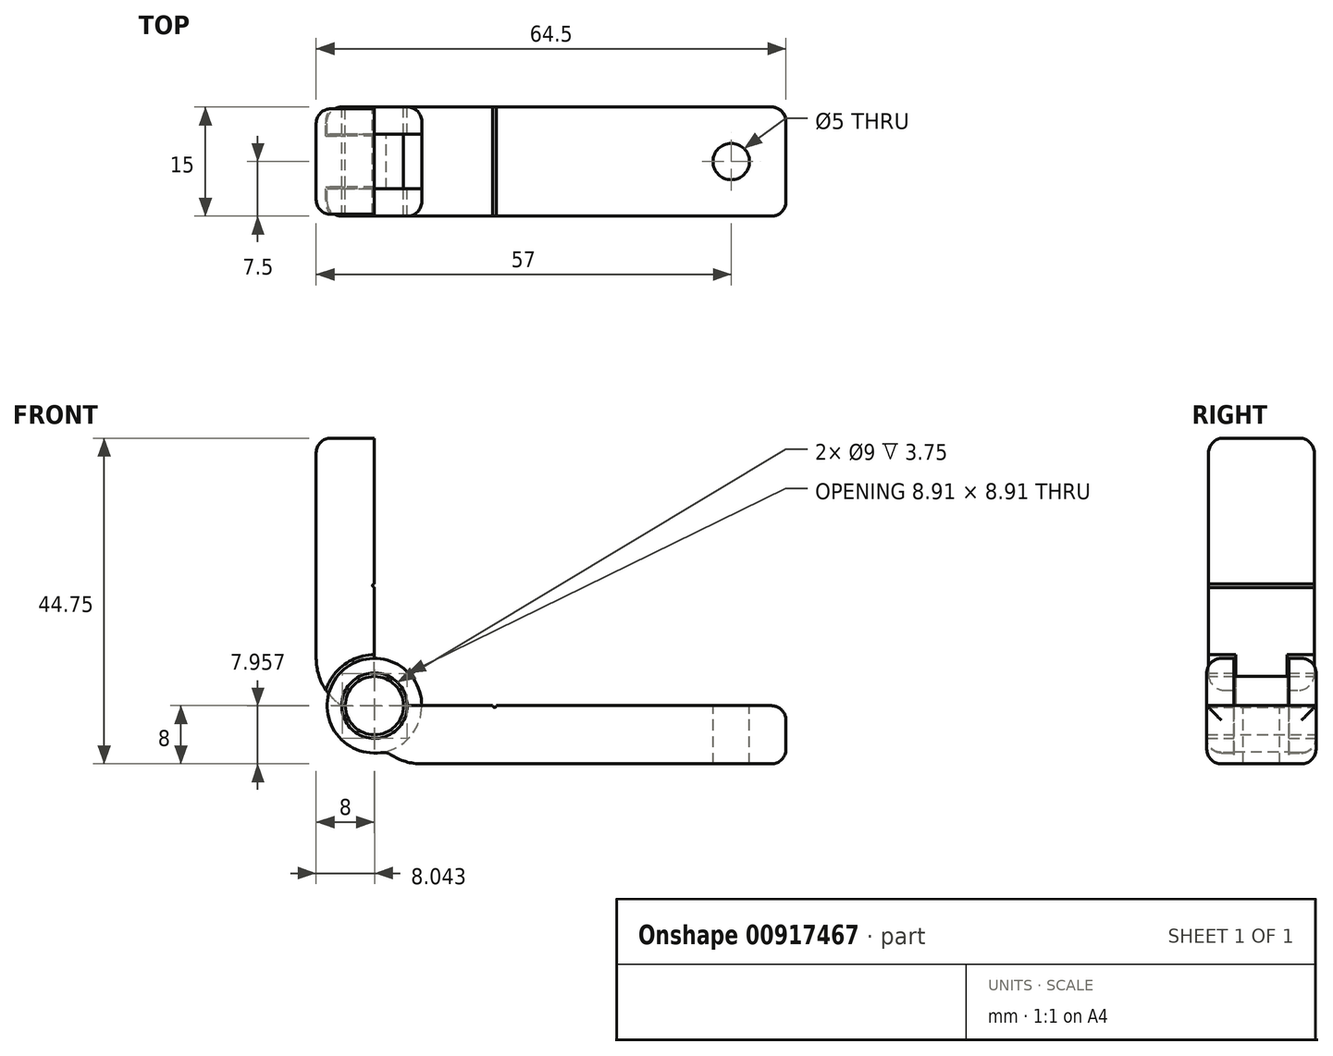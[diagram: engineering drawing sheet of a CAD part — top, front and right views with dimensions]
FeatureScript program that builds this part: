
annotation { "Feature Type Name" : "Feature", "Feature Type Description" : "" }
export const myFeature = defineFeature(function(context is Context, id is Id, definition is map)
    precondition{}
    {
        {
            var Q0;
            Q0=qCreatedBy(makeId("Front.planeOp"),FACE);
            var sketch = newSketch(context, id + "F0", { "sketchPlane" : qUnion([Q0])});
            skLineSegment(sketch, "E0.bottom", {"start": v(0, 0) * mm, "end": v(50, 0) * mm});
            skLineSegment(sketch, "E0.top", {"start": v(0, 8) * mm, "end": v(9.75, 8) * mm});
            skLineSegment(sketch, "E0.left", {"start": v(0, 0) * mm, "end": v(0, 8) * mm});
            skLineSegment(sketch, "E0.right", {"start": v(50, 0) * mm, "end": v(50, 8) * mm});
            skArc(sketch, "E1", {"start": v(9.75, 8) * mm, "mid": v(10, 7.75) * mm, "end": v(10.25, 8) * mm});
            skLineSegment(sketch, "E2.trimOffspring", {"start": v(10.25, 8) * mm, "end": v(50, 8) * mm});
            skLineSegment(sketch, "E3", {"start": v(0, 8) * mm, "end": v(-31.98, 8) * mm, "construction": true});
            skCircle(sketch, "E4", {"center": v(-6.5, 8) * mm, "radius": 4 * mm});
            skCircle(sketch, "E5", {"center": v(-6.5, 8) * mm, "radius": 4.5 * mm});
            skPoint(sketch, "E6", {"position": v(-2, 8) * mm});
            skPoint(sketch, "E7", {"position": v(-6.5, 12.5) * mm});
            skLineSegment(sketch, "E8.bottom", {"start": v(-6.5, 14.5) * mm, "end": v(-14.5, 14.5) * mm});
            skLineSegment(sketch, "E8.top", {"start": v(-6.5, 44.75) * mm, "end": v(-14.5, 44.75) * mm});
            skLineSegment(sketch, "E8.left", {"start": v(-6.5, 14.5) * mm, "end": v(-6.5, 24.25) * mm});
            skLineSegment(sketch, "E8.right", {"start": v(-14.5, 14.5) * mm, "end": v(-14.5, 44.75) * mm});
            skArc(sketch, "E9", {"start": v(-6.5, 24.75) * mm, "mid": v(-6.75, 24.5) * mm, "end": v(-6.5, 24.25) * mm});
            skLineSegment(sketch, "E10.trimOffspring", {"start": v(-6.5, 24.75) * mm, "end": v(-6.5, 44.75) * mm});
            skLineSegment(sketch, "E11", {"start": v(-2, 8) * mm, "end": v(0, 8) * mm});
            skPoint(sketch, "E12", {"position": v(-6.5, 3.5) * mm});
            skArc(sketch, "E13", {"start": v(-6.5, 3.5) * mm, "mid": v(-3.7, 0.93) * mm, "end": v(0, 0) * mm});
            skPoint(sketch, "E14", {"position": v(-11, 8) * mm});
            skArc(sketch, "E15", {"start": v(-14.5, 14.5) * mm, "mid": v(-13.57, 10.8) * mm, "end": v(-11, 8) * mm});
            skLineSegment(sketch, "E16", {"start": v(-6.5, 12.5) * mm, "end": v(-6.5, 14.5) * mm});
            skLineSegment(sketch, "E17", {"start": v(-6.5, 12.5) * mm, "end": v(-6.5, 12) * mm});
            skLineSegment(sketch, "E18", {"start": v(-11, 8) * mm, "end": v(-10.5, 8) * mm});
            skCircle(sketch, "E19", {"center": v(-6.5, 8) * mm, "radius": 6.5 * mm});
            skSolve(sketch);
        }
        {
            var Q0;
            Q0=makeQuery(id+"F0.imprint","IMPRINT",FACE,{"disambiguationData":[TD([[makeQuery(id+"F0.imprint","IMPRINT",EDGE,{"derivedFrom":sQuery(id+"F0.wireOp",EDGE,"E0.bottom")}),1.0]])]});
            var Q1;
            Q1=makeQuery(id+"F0.imprint","IMPRINT",FACE,{"disambiguationData":[TD([[makeQuery(id+"F0.imprint","IMPRINT",EDGE,{"derivedFrom":sQuery(id+"F0.wireOp",EDGE,"E0.left")}),1.0]])]});
            var Q2;
            {var subQ0=sQuery(id+"F0.wireOp",EDGE,"E11");Q2=makeQuery(id+"F0.imprint","IMPRINT",FACE,{"disambiguationData":[TD([[makeQuery(id+"F0.imprint","IMPRINT",EDGE,{"derivedFrom":subQ0}),-1.0]])]});}
            var Q3;
            {var subQ0=sQuery(id+"F0.wireOp",EDGE,"E11");Q3=makeQuery(id+"F0.imprint","IMPRINT",FACE,{"disambiguationData":[TD([[makeQuery(id+"F0.imprint","IMPRINT",EDGE,{"derivedFrom":subQ0}),1.0]])]});}
            var Q4;
            {var subQ3=sQuery(id+"F0.wireOp",EDGE,"E16");Q4=makeQuery(id+"F0.imprint","IMPRINT",FACE,{"disambiguationData":[TD([[makeQuery(id+"F0.imprint","IMPRINT",EDGE,{"derivedFrom":subQ3}),1.0]])]});}
            var Q5;
            {var subQ0=sQuery(id+"F0.wireOp",EDGE,"E13");var subQ1=sQuery(id+"F0.wireOp",EDGE,"E5");var subQ2=makeQuery(id+"F0.imprint","INTERSECT",VERTEX,{"derivedFrom":[subQ1,subQ0]});Q5=makeQuery(id+"F0.imprint","IMPRINT",FACE,{"disambiguationData":[TD([[makeQuery(id+"F0.imprint","IMPRINT",EDGE,{"disambiguationData":[TD([[subQ2,-1.0]])],"derivedFrom":subQ0}),-1.0]])]});}
            extrude(context, id + "F1", {"entities" : qUnion([Q0, Q1, Q2, Q3, Q4, Q5]), "depth" : 7.5 * mm, "offsetDistance" : 25 * mm, "hasSecondDirection" : true, "secondDirectionOppositeDirection" : true, "secondDirectionDepth" : 7.5 * mm});
        }
        {
            var Q0;
            {var subQ0=sQuery(id+"F0.wireOp",EDGE,"E11");Q0=makeQuery(id+"F0.imprint","IMPRINT",FACE,{"disambiguationData":[TD([[makeQuery(id+"F0.imprint","IMPRINT",EDGE,{"derivedFrom":subQ0}),1.0]])]});}
            var Q1;
            {var subQ3=sQuery(id+"F0.wireOp",EDGE,"E16");Q1=makeQuery(id+"F0.imprint","IMPRINT",FACE,{"disambiguationData":[TD([[makeQuery(id+"F0.imprint","IMPRINT",EDGE,{"derivedFrom":subQ3}),1.0]])]});}
            var Q2;
            {var subQ0=sQuery(id+"F0.wireOp",EDGE,"E13");var subQ1=sQuery(id+"F0.wireOp",EDGE,"E5");var subQ2=makeQuery(id+"F0.imprint","INTERSECT",VERTEX,{"derivedFrom":[subQ1,subQ0]});Q2=makeQuery(id+"F0.imprint","IMPRINT",FACE,{"disambiguationData":[TD([[makeQuery(id+"F0.imprint","IMPRINT",EDGE,{"disambiguationData":[TD([[subQ2,-1.0]])],"derivedFrom":subQ0}),-1.0]])]});}
            var Q3;
            {var subQ0=sQuery(id+"F0.wireOp",EDGE,"E11");Q3=makeQuery(id+"F0.imprint","IMPRINT",FACE,{"disambiguationData":[TD([[makeQuery(id+"F0.imprint","IMPRINT",EDGE,{"derivedFrom":subQ0}),-1.0]])]});}
            extrude(context, id + "F2", {"entities" : qUnion([Q0, Q1, Q2, Q3]), "operationType" : NewBodyOperationType.REMOVE, "oppositeDirection" : true, "depth" : 3.75 * mm, "offsetDistance" : 25 * mm, "hasSecondDirection" : true, "secondDirectionOppositeDirection" : false, "secondDirectionDepth" : 3.75 * mm});
        }
        {
            var Q0;
            Q0=makeQuery(id+"F0.imprint","IMPRINT",FACE,{"disambiguationData":[TD([[makeQuery(id+"F0.imprint","IMPRINT",EDGE,{"derivedFrom":sQuery(id+"F0.wireOp",EDGE,"E8.bottom")}),-1.0]])]});
            var Q1;
            Q1=makeQuery(id+"F0.imprint","IMPRINT",FACE,{"disambiguationData":[TD([[makeQuery(id+"F0.imprint","IMPRINT",EDGE,{"derivedFrom":sQuery(id+"F0.wireOp",EDGE,"E8.bottom")}),1.0]])]});
            var Q2;
            {var subQ3=sQuery(id+"F0.wireOp",EDGE,"E16");Q2=makeQuery(id+"F0.imprint","IMPRINT",FACE,{"disambiguationData":[TD([[makeQuery(id+"F0.imprint","IMPRINT",EDGE,{"derivedFrom":subQ3}),1.0]])]});}
            var Q3;
            {var subQ0=sQuery(id+"F0.wireOp",EDGE,"E4");var subQ1=makeQuery(id+"F0.imprint","INTERSECT",VERTEX,{"derivedFrom":[subQ0,sQuery(id+"F0.wireOp",EDGE,"E17")]});Q3=makeQuery(id+"F0.imprint","IMPRINT",FACE,{"disambiguationData":[TD([[makeQuery(id+"F0.imprint","IMPRINT",EDGE,{"disambiguationData":[TD([[subQ1,-1.0]])],"derivedFrom":subQ0}),1.0]])]});}
            var Q4;
            {var subQ0=sQuery(id+"F0.wireOp",EDGE,"E17");Q4=makeQuery(id+"F0.imprint","IMPRINT",FACE,{"disambiguationData":[TD([[makeQuery(id+"F0.imprint","IMPRINT",EDGE,{"derivedFrom":subQ0}),-1.0]])]});}
            extrude(context, id + "F3", {"entities" : qUnion([Q0, Q1, Q2, Q3, Q4]), "depth" : 3.5 * mm, "offsetDistance" : 25 * mm, "hasSecondDirection" : true, "secondDirectionOppositeDirection" : true, "secondDirectionDepth" : 3.5 * mm});
        }
        {
            var Q0;
            {var subQ0=sQuery(id+"F0.wireOp",EDGE,"E4");var subQ1=makeQuery(id+"F0.imprint","INTERSECT",VERTEX,{"derivedFrom":[subQ0,sQuery(id+"F0.wireOp",EDGE,"E17")]});Q0=makeQuery(id+"F0.imprint","IMPRINT",FACE,{"disambiguationData":[TD([[makeQuery(id+"F0.imprint","IMPRINT",EDGE,{"disambiguationData":[TD([[subQ1,-1.0]])],"derivedFrom":subQ0}),1.0]])]});}
            extrude(context, id + "F4", {"entities" : qUnion([Q0]), "operationType" : NewBodyOperationType.ADD, "depth" : 7.5 * mm, "offsetDistance" : 25 * mm, "hasSecondDirection" : true, "secondDirectionOppositeDirection" : true, "secondDirectionDepth" : 7.5 * mm});
        }
        {
            var Q0;
            Q0=makeQuery(id+"F3.opExtrude","CAP_FACE",FACE,{"disambiguationData":[OSD([sQuery(id+"F0.wireOp",EDGE,"E4"),sQuery(id+"F0.wireOp",EDGE,"E8.top"),sQuery(id+"F0.wireOp",EDGE,"E8.left"),sQuery(id+"F0.wireOp",EDGE,"E8.right"),sQuery(id+"F0.wireOp",EDGE,"E9"),sQuery(id+"F0.wireOp",EDGE,"E10.trimOffspring"),sQuery(id+"F0.wireOp",EDGE,"E15"),sQuery(id+"F0.wireOp",EDGE,"E16"),sQuery(id+"F0.wireOp",EDGE,"E17"),sQuery(id+"F0.wireOp",EDGE,"E18")])],"isStart":false});
            var sketch = newSketch(context, id + "F5", { "sketchPlane" : qUnion([Q0])});
            skLineSegment(sketch, "E20.top", {"start": v(-6.5, 44.75) * mm, "end": v(-14.5, 44.75) * mm});
            skLineSegment(sketch, "E20.left", {"start": v(-6.5, 15) * mm, "end": v(-6.5, 24.25) * mm});
            skLineSegment(sketch, "E20.right", {"start": v(-14.5, 14.5) * mm, "end": v(-14.5, 44.75) * mm});
            skArc(sketch, "E21", {"start": v(-6.5, 24.75) * mm, "mid": v(-6.75, 24.5) * mm, "end": v(-6.5, 24.25) * mm});
            skLineSegment(sketch, "E22.trimOffspring", {"start": v(-6.5, 24.75) * mm, "end": v(-6.5, 44.75) * mm});
            skArc(sketch, "E23", {"start": v(-6.5, 15) * mm, "mid": v(-10.62, 13.66) * mm, "end": v(-13.16, 10.14) * mm});
            skArc(sketch, "E24", {"start": v(-14.5, 14.5) * mm, "mid": v(-14.16, 12.22) * mm, "end": v(-13.16, 10.14) * mm});
            skSolve(sketch);
        }
        {
            var Q0;
            Q0 = qSketchRegion(id + "F5", true);
            extrude(context, id + "F6", {"entities" : qUnion([Q0]), "operationType" : NewBodyOperationType.ADD, "depth" : 3.75 * mm, "offsetDistance" : 25 * mm, "hasSecondDirection" : true, "secondDirectionOppositeDirection" : true, "secondDirectionDepth" : 10.75 * mm});
        }
        {
            var Q0;
            Q0=makeQuery(id+"F1.opExtrude","CAP_EDGE",EDGE,{"disambiguationData":[OSD([sQuery(id+"F0.wireOp",EDGE,"E0.right")])],"isStart":false});
            var Q1;
            Q1=makeQuery(id+"F1.opExtrude","CAP_EDGE",EDGE,{"disambiguationData":[OSD([sQuery(id+"F0.wireOp",EDGE,"E0.right")])],"isStart":true});
            var Q2;
            Q2=makeQuery(id+"F1.opExtrude","SWEPT_EDGE",EDGE,{"disambiguationData":[OSD([sQuery(id+"F0.wireOp",EDGE,"E0.right"),sQuery(id+"F0.wireOp",EDGE,"E2.trimOffspring")])]});
            var Q3;
            Q3=makeQuery(id+"F1.opExtrude","SWEPT_EDGE",EDGE,{"disambiguationData":[OSD([sQuery(id+"F0.wireOp",EDGE,"E0.bottom"),sQuery(id+"F0.wireOp",EDGE,"E0.right")])]});
            var Q4;
            Q4=makeQuery(id+"F1.opExtrude","CAP_EDGE",EDGE,{"disambiguationData":[OSD([sQuery(id+"F0.wireOp",EDGE,"E0.bottom")])],"isStart":false});
            var Q5;
            Q5=makeQuery(id+"F1.opExtrude","CAP_EDGE",EDGE,{"disambiguationData":[OSD([sQuery(id+"F0.wireOp",EDGE,"E19")])],"isStart":false});
            var Q6;
            Q6=makeQuery(id+"F1.opExtrude","CAP_EDGE",EDGE,{"disambiguationData":[OSD([sQuery(id+"F0.wireOp",EDGE,"E0.bottom")])],"isStart":true});
            var Q7;
            Q7=makeQuery(id+"F1.opExtrude","CAP_EDGE",EDGE,{"disambiguationData":[OSD([sQuery(id+"F0.wireOp",EDGE,"E19")])],"isStart":true});
            var Q8;
            Q8=makeQuery(id+"F6.opExtrude","CAP_EDGE",EDGE,{"disambiguationData":[OSD([sQuery(id+"F5.wireOp",EDGE,"E20.right")])],"isStart":true});
            var Q9;
            Q9=makeQuery(id+"F6.opExtrude","CAP_EDGE",EDGE,{"disambiguationData":[OSD([sQuery(id+"F5.wireOp",EDGE,"E20.top")])],"isStart":true});
            var Q10;
            Q10=makeQuery(id+"F6.boolean.opBoolean","MERGE",EDGE,{"derivedFrom":[makeQuery(id+"F3.opExtrude","SWEPT_EDGE",EDGE,{"disambiguationData":[OSD([sQuery(id+"F0.wireOp",EDGE,"E8.top"),sQuery(id+"F0.wireOp",EDGE,"E8.right")])]}),makeQuery(id+"F6.opExtrude","SWEPT_EDGE",EDGE,{"disambiguationData":[OSD([sQuery(id+"F5.wireOp",EDGE,"E20.top"),sQuery(id+"F5.wireOp",EDGE,"E20.right")])]})]});
            var Q11;
            Q11=makeQuery(id+"F6.opExtrude","CAP_EDGE",EDGE,{"disambiguationData":[OSD([sQuery(id+"F5.wireOp",EDGE,"E20.top")])],"isStart":false});
            var Q12;
            Q12=makeQuery(id+"F6.opExtrude","CAP_EDGE",EDGE,{"disambiguationData":[OSD([sQuery(id+"F5.wireOp",EDGE,"E20.right")])],"isStart":false});
            var Q13;
            {var subQ0=sQuery(id+"F0.wireOp",EDGE,"E13");var subQ1=sQuery(id+"F0.wireOp",EDGE,"E19");Q13=makeQuery(id+"F2.boolean.opBoolean","SPLIT",EDGE,{"disambiguationData":[topologyDisambiguationEdgeConnected([makeQuery(id+"F1.opExtrude","SWEPT_FACE",FACE,{"disambiguationData":[OSD([subQ0])]}),makeQuery(id+"F2.opExtrude","SWEPT_FACE",FACE,{"disambiguationData":[OSD([subQ1])]})])],"derivedFrom":makeQuery(id+"F1.opExtrude","SWEPT_EDGE",EDGE,{"disambiguationData":[OSD([subQ0,subQ1])]})});}
            fillet(context, id + "F7", {"entities" : qUnion([Q0, Q1, Q2, Q3, Q4, Q5, Q6, Q7, Q8, Q9, Q10, Q11, Q12, Q13]), "radius" : 2 * mm, "tangentPropagation" : true, "allowEdgeOverflow" : false});
        }
        {
            var Q0;
            Q0=makeQuery(id+"F1.opExtrude","SWEPT_FACE",FACE,{"disambiguationData":[OSD([sQuery(id+"F0.wireOp",EDGE,"E2.trimOffspring")])]});
            var sketch = newSketch(context, id + "F8", { "sketchPlane" : qUnion([Q0])});
            skCircle(sketch, "E25", {"center": v(42.5, 0) * mm, "radius": 2.5 * mm});
            skSolve(sketch);
        }
        {
            var Q0;
            Q0 = qSketchRegion(id + "F8", true);
            extrude(context, id + "F9", {"entities" : qUnion([Q0]), "operationType" : NewBodyOperationType.REMOVE, "oppositeDirection" : true, "depth" : 25 * mm, "offsetDistance" : 25 * mm});
        }
    });
